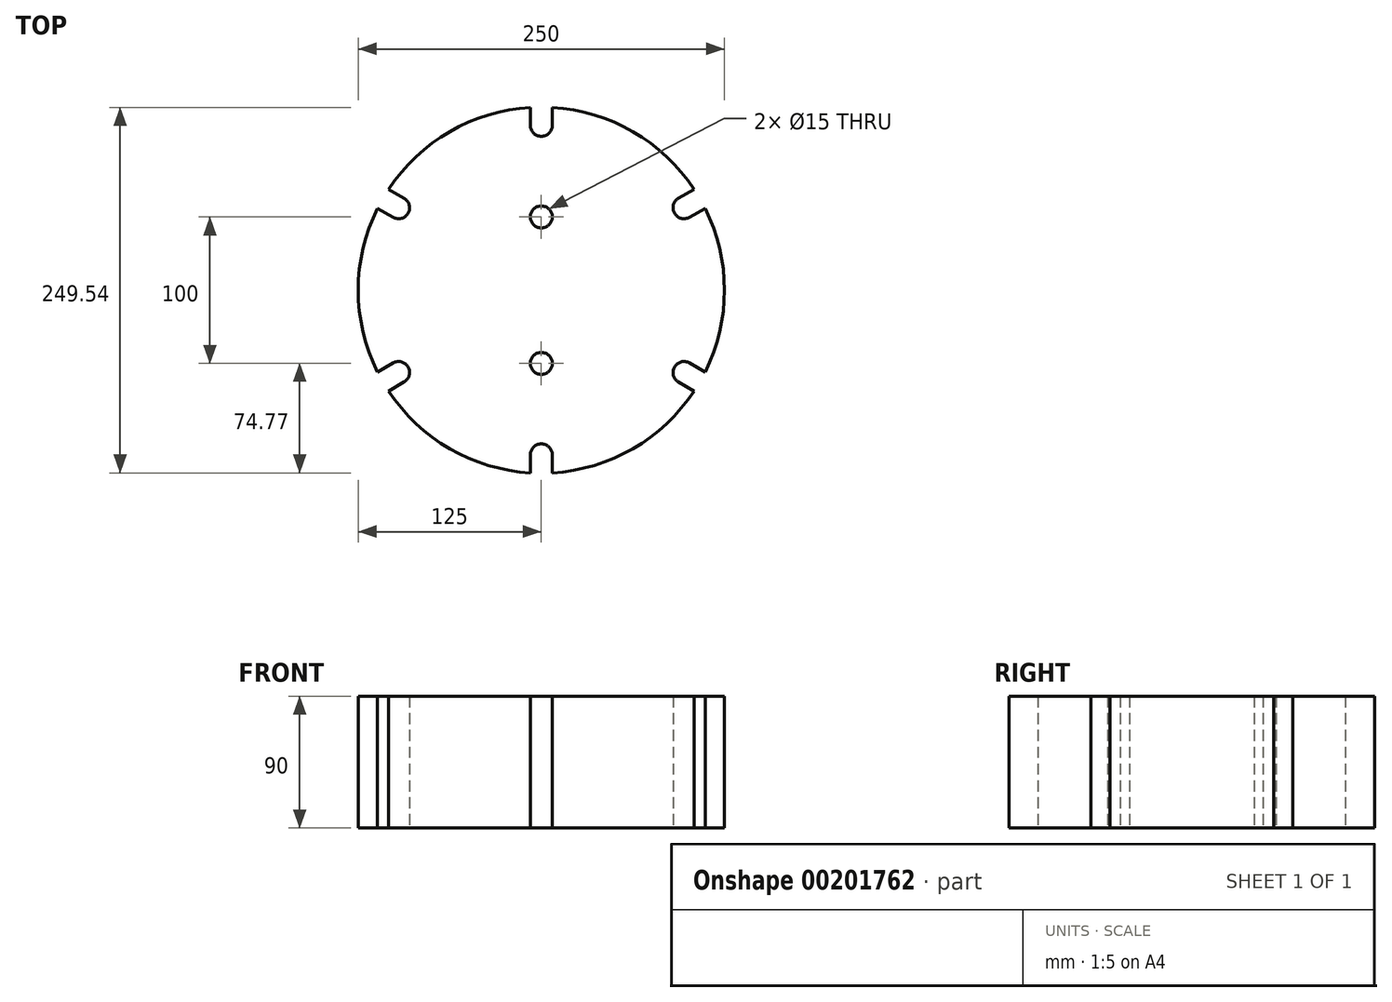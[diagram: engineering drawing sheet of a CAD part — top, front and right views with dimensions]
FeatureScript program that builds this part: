
annotation { "Feature Type Name" : "Feature", "Feature Type Description" : "" }
export const myFeature = defineFeature(function(context is Context, id is Id, definition is map)
    precondition{}
    {
        {
            var Q0;
            Q0=qCreatedBy(makeId("Top.planeOp"),FACE);
            var sketch = newSketch(context, id + "F0", { "sketchPlane" : qUnion([Q0])});
            skArc(sketch, "E0", {"start": v(-7.5, 124.77) * mm, "mid": v(-62.5, 108.25) * mm, "end": v(-104.3, 68.88) * mm});
            skCircle(sketch, "E1", {"center": v(0, 0) * mm, "radius": 112.5 * mm, "construction": true});
            skLineSegment(sketch, "E2", {"start": v(0, 112.5) * mm, "end": v(0, 125) * mm});
            skArc(sketch, "E3.0.startCap", {"start": v(7.5, 112.5) * mm, "mid": v(0, 105) * mm, "end": v(-7.5, 112.5) * mm});
            skLineSegment(sketch, "E3.0.left", {"start": v(-7.5, 112.5) * mm, "end": v(-7.5, 125) * mm});
            skLineSegment(sketch, "E3.0.right", {"start": v(7.5, 112.5) * mm, "end": v(7.5, 125) * mm});
            skLineSegment(sketch, "E4.1.1", {"start": v(-93.68, 62.75) * mm, "end": v(-104.5, 69) * mm});
            skArc(sketch, "E4.1.2", {"start": v(-93.68, 62.75) * mm, "mid": v(-90.93, 52.5) * mm, "end": v(-101.18, 49.75) * mm});
            skLineSegment(sketch, "E4.1.3", {"start": v(-101.18, 49.75) * mm, "end": v(-112, 56) * mm});
            skLineSegment(sketch, "E4.2.1", {"start": v(-101.18, -49.75) * mm, "end": v(-112, -56) * mm});
            skArc(sketch, "E4.2.2", {"start": v(-101.18, -49.75) * mm, "mid": v(-90.93, -52.5) * mm, "end": v(-93.68, -62.75) * mm});
            skLineSegment(sketch, "E4.2.3", {"start": v(-93.68, -62.75) * mm, "end": v(-104.5, -69) * mm});
            skLineSegment(sketch, "E4.3.1", {"start": v(-7.5, -112.5) * mm, "end": v(-7.5, -125) * mm});
            skArc(sketch, "E4.3.2", {"start": v(-7.5, -112.5) * mm, "mid": v(0, -105) * mm, "end": v(7.5, -112.5) * mm});
            skLineSegment(sketch, "E4.3.3", {"start": v(7.5, -112.5) * mm, "end": v(7.5, -125) * mm});
            skLineSegment(sketch, "E4.4.1", {"start": v(93.68, -62.75) * mm, "end": v(104.5, -69) * mm});
            skArc(sketch, "E4.4.2", {"start": v(93.68, -62.75) * mm, "mid": v(90.93, -52.5) * mm, "end": v(101.18, -49.75) * mm});
            skLineSegment(sketch, "E4.4.3", {"start": v(101.18, -49.75) * mm, "end": v(112, -56) * mm});
            skLineSegment(sketch, "E4.5.1", {"start": v(101.18, 49.75) * mm, "end": v(112, 56) * mm});
            skArc(sketch, "E4.5.2", {"start": v(101.18, 49.75) * mm, "mid": v(90.93, 52.5) * mm, "end": v(93.68, 62.75) * mm});
            skLineSegment(sketch, "E4.5.3", {"start": v(93.68, 62.75) * mm, "end": v(104.5, 69) * mm});
            skArc(sketch, "E5.trimOffspring", {"start": v(104.3, 68.88) * mm, "mid": v(62.5, 108.25) * mm, "end": v(7.5, 124.77) * mm});
            skArc(sketch, "E6.trimOffspring", {"start": v(-111.8, 55.9) * mm, "mid": v(-125, 0) * mm, "end": v(-111.8, -55.9) * mm});
            skArc(sketch, "E7.trimOffspring", {"start": v(-104.3, -68.88) * mm, "mid": v(-62.5, -108.25) * mm, "end": v(-7.5, -124.77) * mm});
            skArc(sketch, "E8.trimOffspring", {"start": v(7.5, -124.77) * mm, "mid": v(62.5, -108.25) * mm, "end": v(104.3, -68.88) * mm});
            skArc(sketch, "E9.trimOffspring", {"start": v(111.8, -55.9) * mm, "mid": v(125, 0) * mm, "end": v(111.8, 55.9) * mm});
            skCircle(sketch, "E10", {"center": v(0, 50) * mm, "radius": 7.5 * mm});
            skCircle(sketch, "E11", {"center": v(0, -50) * mm, "radius": 7.5 * mm});
            skSolve(sketch);
        }
        {
            var Q0;
            {var subQ17=sQuery(id+"F0.wireOp",EDGE,"E0");Q0=makeQuery(id+"F0.imprint","IMPRINT",FACE,{"disambiguationData":[TD([[makeQuery(id+"F0.imprint","IMPRINT",EDGE,{"derivedFrom":subQ17}),1.0]])]});}
            extrude(context, id + "F1", {"entities" : qUnion([Q0]), "depth" : 90 * mm});
        }
        {
            var Q0;
            Q0=makeQuery(id+"F1.opExtrude","SWEPT_BODY",BODY,{"disambiguationData":[OSD([sQuery(id+"F0.wireOp",EDGE,"E0"),sQuery(id+"F0.wireOp",EDGE,"E3.0.startCap"),sQuery(id+"F0.wireOp",EDGE,"E3.0.left"),sQuery(id+"F0.wireOp",EDGE,"E3.0.right"),sQuery(id+"F0.wireOp",EDGE,"E4.1.1"),sQuery(id+"F0.wireOp",EDGE,"E4.1.2"),sQuery(id+"F0.wireOp",EDGE,"E4.1.3"),sQuery(id+"F0.wireOp",EDGE,"E4.2.1"),sQuery(id+"F0.wireOp",EDGE,"E4.2.2"),sQuery(id+"F0.wireOp",EDGE,"E4.2.3"),sQuery(id+"F0.wireOp",EDGE,"E4.3.1"),sQuery(id+"F0.wireOp",EDGE,"E4.3.2"),sQuery(id+"F0.wireOp",EDGE,"E4.3.3"),sQuery(id+"F0.wireOp",EDGE,"E4.4.1"),sQuery(id+"F0.wireOp",EDGE,"E4.4.2"),sQuery(id+"F0.wireOp",EDGE,"E4.4.3"),sQuery(id+"F0.wireOp",EDGE,"E4.5.1"),sQuery(id+"F0.wireOp",EDGE,"E4.5.2"),sQuery(id+"F0.wireOp",EDGE,"E4.5.3"),sQuery(id+"F0.wireOp",EDGE,"E5.trimOffspring"),sQuery(id+"F0.wireOp",EDGE,"E6.trimOffspring"),sQuery(id+"F0.wireOp",EDGE,"E7.trimOffspring"),sQuery(id+"F0.wireOp",EDGE,"E8.trimOffspring"),sQuery(id+"F0.wireOp",EDGE,"E9.trimOffspring"),sQuery(id+"F0.wireOp",EDGE,"E10"),sQuery(id+"F0.wireOp",EDGE,"E11")])]});
            transform(context, id + "F2", {"entities" : qUnion([Q0]), "transformType" : TransformType.TRANSLATION_3D, "dx" : 0 * mm, "dy" : 0 * mm, "dz" : -90 * mm, "makeCopy" : false});
        }
    });
